# Revit family: Kühlschrank-Tiefkühlung Glastür 590L-Melios - Eigen
name_source: partatom
category: Sonderausstattung
revit_build: Autodesk Revit 2015 (Build: 20140606_1530(x64)
units: mm (PartAtom-declared; Revit-internal decimal feet)

## types (1)
- BR 590 - 720 x 840 x 2050
    Artikelnr. = HKMTV59-ME
    Breite = 720 mm  [stored 2.3622 ft]
    Dichtung Stärke = 20 mm  [stored 0.0656168 ft]
    Elektroanschluss Abstand Seite = 250 mm  [stored 0.82021 ft]
    Elektroanschluss Höhe = 1800 mm  [stored 5.90551 ft]
    Energieeffizienzklasse = D
    Energieverbrauch = 5,25 kWh/24h
    Füße Abstand Hinten = 82 mm  [stored 0.269029 ft]
    Füße Abstand Seiten = 90 mm  [stored 0.295276 ft]
    Füße Abstand Vorne = 50 mm  [stored 0.164042 ft]
    Glas = Glas
    Griff = Stahl, verchromt
    Hersteller = CoolCompact
    Kapazität = 23 x GN2/1
    Kopfteil Höhe = 337 mm  [stored 1.10564 ft]
    Kopfteil Tiefe = 70 mm  [stored 0.229659 ft]
    Kopfteil Verlängerung = 26 mm
    Korpus Höhe = 1563 mm  [stored 5.12795 ft]
    Korpus Tiefe = 760 mm
    Kälteleistung = 560W bei -30°C VT/+32°C UT
    Kältemittel = R290
    Material = Edelstahl AISI 304
    Netzkabellänge = 2500 mm  [stored 8.2021 ft]
    Pole = 1
    Scheinleistung = 0 VA
    Sockelhöhe = 150 mm
    Spannung = 230 V
    Temp. Bereich = -15°C / -22°C
    Türabstand Links = 22 mm
    Türabstand Oben = 8 mm  [stored 0.0262467 ft]
    Türabstand Rechts = 22 mm
    Türabstand Unten = 50 mm  [stored 0.164042 ft]
    Türen Anzahl = 1
    Türen Breite = 677 mm  [stored 2.22113 ft]
    Türen Höhe = 1479 mm  [stored 4.85236 ft]
    Türen Stärke = 40 mm  [stored 0.131234 ft]
    Wandstärke Hinten = 65 mm  [stored 0.213255 ft]
    Wandstärke Oben = 95 mm
    Wandstärke Seiten = 93 mm  [stored 0.305118 ft]
    Wandstärke Unten = 90 mm  [stored 0.295276 ft]
    Watt = 400 W

note: [stored X ft] marks values corroborated as IEEE doubles in the binary element streams (Revit-internal decimal feet)

## geometry (parser evidence)
native form markers: Blend x15, Sweep x1
no freeform markers — native parametric forms only
